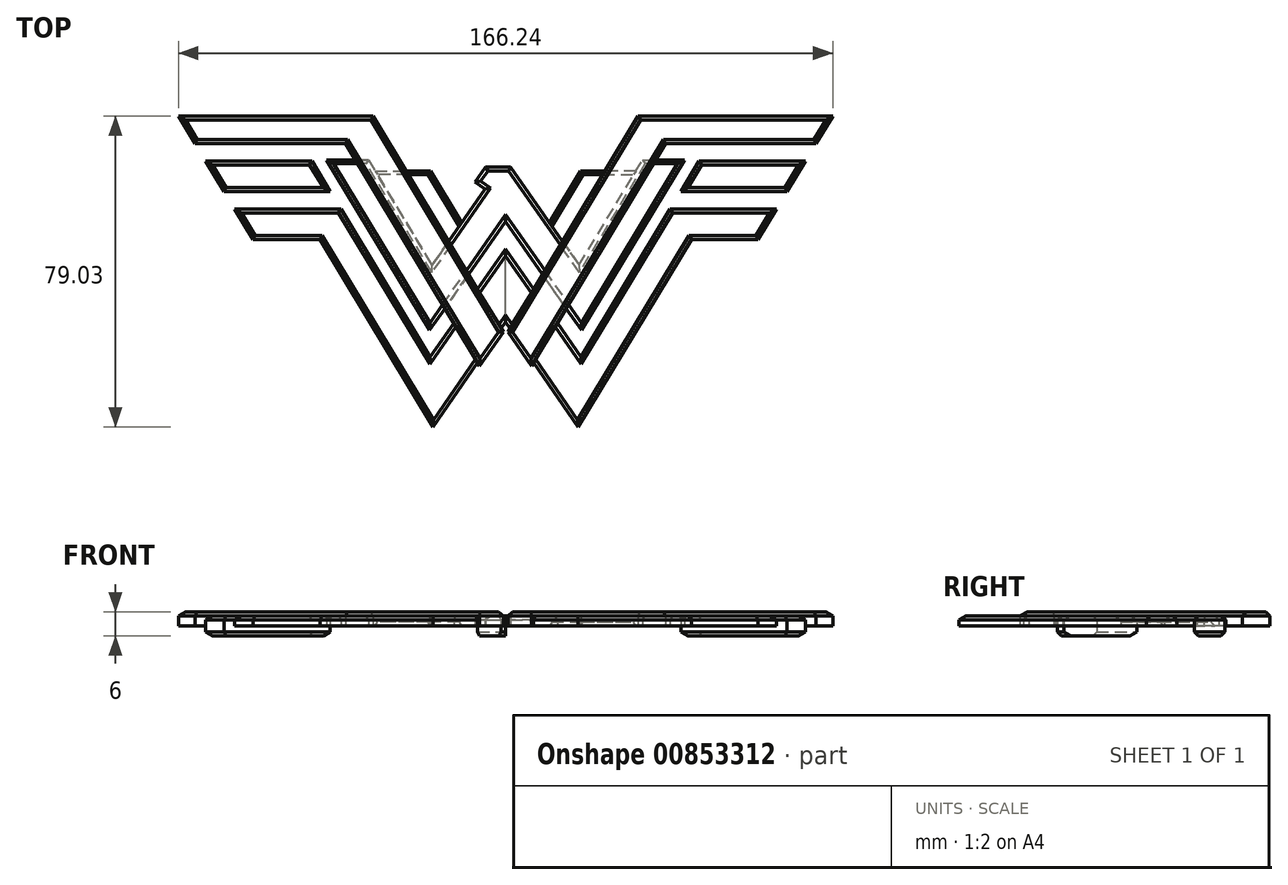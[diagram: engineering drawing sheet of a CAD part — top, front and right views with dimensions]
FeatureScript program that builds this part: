
annotation { "Feature Type Name" : "Feature", "Feature Type Description" : "" }
export const myFeature = defineFeature(function(context is Context, id is Id, definition is map)
    precondition{}
    {
        {
            var Q0;
            Q0=qCreatedBy(makeId("Top.planeOp"),FACE);
            var sketch = newSketch(context, id + "F0", { "sketchPlane" : qUnion([Q0])});
            skLineSegment(sketch, "E0", {"start": v(-1.3, 32.97) * mm, "end": v(-18.68, 8.07) * mm});
            skLineSegment(sketch, "E1", {"start": v(-18.68, 8.07) * mm, "end": v(-34.82, 34.82) * mm});
            skLineSegment(sketch, "E2", {"start": v(-34.82, 34.82) * mm, "end": v(-45.43, 34.82) * mm});
            skLineSegment(sketch, "E3", {"start": v(-45.43, 34.82) * mm, "end": v(-29.28, 8.07) * mm});
            skLineSegment(sketch, "E4", {"start": v(-29.28, 8.07) * mm, "end": v(-24.4, 0) * mm});
            skLineSegment(sketch, "E5", {"start": v(-24.4, 0) * mm, "end": v(-19.3, -8.47) * mm});
            skLineSegment(sketch, "E6", {"start": v(-19.3, -8.47) * mm, "end": v(0, 19.16) * mm});
            skLineSegment(sketch, "E7", {"start": v(0, 19.16) * mm, "end": v(0, 32.97) * mm});
            skLineSegment(sketch, "E8", {"start": v(-33.13, 32.02) * mm, "end": v(-19.08, 32.02) * mm});
            skLineSegment(sketch, "E9", {"start": v(-19.08, 32.02) * mm, "end": v(-11.14, 18.87) * mm});
            skLineSegment(sketch, "E10.MirrorCS", {"start": v(1.3, 32.97) * mm, "end": v(18.68, 8.07) * mm});
            skLineSegment(sketch, "E11.MirrorCS", {"start": v(19.3, -8.47) * mm, "end": v(0, 19.16) * mm});
            skLineSegment(sketch, "E12.MirrorCS", {"start": v(29.28, 8.07) * mm, "end": v(24.4, 0) * mm});
            skLineSegment(sketch, "E13.MirrorCS", {"start": v(24.4, 0) * mm, "end": v(19.3, -8.47) * mm});
            skLineSegment(sketch, "E14.MirrorCS", {"start": v(45.43, 34.82) * mm, "end": v(29.28, 8.07) * mm});
            skLineSegment(sketch, "E15.MirrorCS", {"start": v(34.82, 34.82) * mm, "end": v(45.43, 34.82) * mm});
            skLineSegment(sketch, "E16.MirrorCS", {"start": v(18.68, 8.07) * mm, "end": v(34.82, 34.82) * mm});
            skLineSegment(sketch, "E17", {"start": v(1.3, 32.97) * mm, "end": v(-5.04, 32.97) * mm});
            skLineSegment(sketch, "E18", {"start": v(-5.04, 32.97) * mm, "end": v(-7.72, 29.14) * mm});
            skLineSegment(sketch, "E19", {"start": v(-7.72, 29.14) * mm, "end": v(-5.2, 27.38) * mm});
            skPoint(sketch, "E20.orphan", {"position": v(0, 34.82) * mm});
            skSolve(sketch);
        }
        {
            var Q0;
            Q0=qCreatedBy(makeId("Top.planeOp"),FACE);
            var sketch = newSketch(context, id + "F1", { "sketchPlane" : qUnion([Q0])});
            skLineSegment(sketch, "E21", {"start": v(-49.18, 34.5) * mm, "end": v(-76.17, 34.5) * mm});
            skLineSegment(sketch, "E22", {"start": v(-76.17, 34.5) * mm, "end": v(-71.52, 26.8) * mm});
            skLineSegment(sketch, "E23", {"start": v(-71.52, 26.8) * mm, "end": v(-44.53, 26.8) * mm});
            skLineSegment(sketch, "E24", {"start": v(-44.53, 26.8) * mm, "end": v(-49.18, 34.5) * mm});
            skLineSegment(sketch, "E25", {"start": v(-68.81, 22.32) * mm, "end": v(-41.82, 22.32) * mm});
            skLineSegment(sketch, "E26", {"start": v(-41.82, 22.32) * mm, "end": v(-37.17, 14.62) * mm});
            skLineSegment(sketch, "E27", {"start": v(-37.17, 14.62) * mm, "end": v(-64.16, 14.62) * mm});
            skLineSegment(sketch, "E28", {"start": v(-64.16, 14.62) * mm, "end": v(-68.81, 22.32) * mm});
            skLineSegment(sketch, "E29", {"start": v(-71.52, 26.8) * mm, "end": v(-68.81, 22.32) * mm, "construction": true});
            skLineSegment(sketch, "E30", {"start": v(-44.53, 26.8) * mm, "end": v(-41.82, 22.32) * mm, "construction": true});
            skLineSegment(sketch, "E31", {"start": v(-47.17, 14.62) * mm, "end": v(-19.15, -31.8) * mm});
            skLineSegment(sketch, "E32", {"start": v(0, -3.25) * mm, "end": v(0, 12.18) * mm});
            skLineSegment(sketch, "E33", {"start": v(0, 12.18) * mm, "end": v(-19.15, -15.24) * mm});
            skLineSegment(sketch, "E34", {"start": v(-19.15, -15.24) * mm, "end": v(-37.17, 14.62) * mm});
            skLineSegment(sketch, "E35", {"start": v(-37.17, 14.62) * mm, "end": v(-47.17, 14.62) * mm});
            skLineSegment(sketch, "E36", {"start": v(-19.15, -31.8) * mm, "end": v(-18.37, -33.1) * mm});
            skLineSegment(sketch, "E37", {"start": v(-18.37, -33.1) * mm, "end": v(0, -6.41) * mm});
            skLineSegment(sketch, "E38", {"start": v(0, -6.41) * mm, "end": v(0, -3.25) * mm});
            skLineSegment(sketch, "E39", {"start": v(-78.87, 38.99) * mm, "end": v(-51.88, 38.99) * mm});
            skLineSegment(sketch, "E40", {"start": v(-51.88, 38.99) * mm, "end": v(-56.07, 45.93) * mm});
            skLineSegment(sketch, "E41", {"start": v(-56.07, 45.93) * mm, "end": v(-83.12, 45.93) * mm});
            skLineSegment(sketch, "E42", {"start": v(-83.12, 45.93) * mm, "end": v(-78.87, 38.99) * mm});
            skLineSegment(sketch, "E43", {"start": v(-51.88, 38.99) * mm, "end": v(-49.18, 34.5) * mm, "construction": true});
            skLineSegment(sketch, "E44", {"start": v(-78.87, 38.99) * mm, "end": v(-76.17, 34.5) * mm, "construction": true});
            skLineSegment(sketch, "E45", {"start": v(-56.07, 45.93) * mm, "end": v(-33.67, 45.93) * mm});
            skLineSegment(sketch, "E46", {"start": v(-33.67, 45.93) * mm, "end": v(-29.48, 38.99) * mm});
            skLineSegment(sketch, "E47", {"start": v(-29.48, 38.99) * mm, "end": v(-51.88, 38.99) * mm});
            skLineSegment(sketch, "E48", {"start": v(-40.68, 38.99) * mm, "end": v(-7.07, -16.69) * mm});
            skLineSegment(sketch, "E49", {"start": v(-29.48, 38.99) * mm, "end": v(-1.1, -8.01) * mm});
            skLineSegment(sketch, "E50", {"start": v(-1.1, -8.01) * mm, "end": v(-0.57, -8.9) * mm});
            skLineSegment(sketch, "E51", {"start": v(-0.57, -8.9) * mm, "end": v(-6.58, -17.5) * mm});
            skLineSegment(sketch, "E52", {"start": v(-6.58, -17.5) * mm, "end": v(-7.07, -16.69) * mm});
            skSolve(sketch);
        }
        {
            var Q0;
            {var subQ4=sQuery(id+"F0.wireOp",EDGE,"E8");Q0=makeQuery(id+"F0.imprint","IMPRINT",FACE,{"disambiguationData":[TD([[makeQuery(id+"F0.imprint","IMPRINT",EDGE,{"derivedFrom":subQ4}),-1.0]])]});}
            extrude(context, id + "F2", {"entities" : qUnion([Q0]), "depth" : 1 * mm, "offsetDistance" : 25 * mm});
        }
        {
            var Q0;
            Q0=makeQuery(id+"F1.imprint","IMPRINT",FACE,{"disambiguationData":[TD([[makeQuery(id+"F1.imprint","IMPRINT",EDGE,{"derivedFrom":sQuery(id+"F1.wireOp",EDGE,"E39")}),1.0]])]});
            var Q1;
            {var subQ3=sQuery(id+"F1.wireOp",EDGE,"E40");Q1=makeQuery(id+"F1.imprint","IMPRINT",FACE,{"disambiguationData":[TD([[makeQuery(id+"F1.imprint","IMPRINT",EDGE,{"derivedFrom":subQ3}),-1.0]])]});}
            var Q2;
            {var subQ0=sQuery(id+"F1.wireOp",EDGE,"E49");var subQ1=sQuery(id+"F1.wireOp",EDGE,"E33");var subQ2=makeQuery(id+"F1.imprint","INTERSECT",VERTEX,{"derivedFrom":[subQ1,subQ0]});Q2=makeQuery(id+"F1.imprint","IMPRINT",FACE,{"disambiguationData":[TD([[makeQuery(id+"F1.imprint","IMPRINT",EDGE,{"disambiguationData":[TD([[subQ2,-1.0]])],"derivedFrom":subQ1}),-1.0]])]});}
            var Q3;
            {var subQ4=sQuery(id+"F1.wireOp",EDGE,"IkarmOyA-QviY-3z2g-ssXT-DGAwllsCsLP8");Q3=makeQuery(id+"F1.imprint","IMPRINT",FACE,{"disambiguationData":[TD([[makeQuery(id+"F1.imprint","IMPRINT",EDGE,{"derivedFrom":subQ4}),-1.0]])]});}
            var Q4;
            {var subQ0=sQuery(id+"F1.wireOp",EDGE,"E49");var subQ1=sQuery(id+"F1.wireOp",EDGE,"E33");var subQ2=makeQuery(id+"F1.imprint","INTERSECT",VERTEX,{"derivedFrom":[subQ1,subQ0]});Q4=makeQuery(id+"F1.imprint","IMPRINT",FACE,{"disambiguationData":[TD([[makeQuery(id+"F1.imprint","IMPRINT",EDGE,{"disambiguationData":[TD([[subQ2,-1.0]])],"derivedFrom":subQ1}),1.0]])]});}
            var Q5;
            {var subQ2=sQuery(id+"F1.wireOp",EDGE,"E50");Q5=makeQuery(id+"F1.imprint","IMPRINT",FACE,{"disambiguationData":[TD([[makeQuery(id+"F1.imprint","IMPRINT",EDGE,{"derivedFrom":subQ2}),-1.0]])]});}
            extrude(context, id + "F3", {"entities" : qUnion([Q0, Q1, Q2, Q3, Q4, Q5]), "depth" : 3.5 * mm, "offsetDistance" : 25 * mm});
        }
        {
            var Q0;
            Q0=makeQuery(id+"F1.imprint","IMPRINT",FACE,{"disambiguationData":[TD([[makeQuery(id+"F1.imprint","IMPRINT",EDGE,{"derivedFrom":sQuery(id+"F1.wireOp",EDGE,"E25")}),-1.0]])]});
            var Q1;
            Q1=makeQuery(id+"F1.imprint","IMPRINT",FACE,{"disambiguationData":[TD([[makeQuery(id+"F1.imprint","IMPRINT",EDGE,{"derivedFrom":sQuery(id+"F1.wireOp",EDGE,"E31")}),1.0]])]});
            var Q2;
            {var subQ5=sQuery(id+"F1.wireOp",EDGE,"E32");Q2=makeQuery(id+"F1.imprint","IMPRINT",FACE,{"disambiguationData":[TD([[makeQuery(id+"F1.imprint","IMPRINT",EDGE,{"derivedFrom":subQ5}),1.0]])]});}
            extrude(context, id + "F4", {"entities" : qUnion([Q0, Q1, Q2]), "depth" : 2.5 * mm, "offsetDistance" : 25 * mm});
        }
        {
            var Q0;
            {var subQ1=sQuery(id+"F0.wireOp",EDGE,"E7");Q0=makeQuery(id+"F0.imprint","IMPRINT",FACE,{"disambiguationData":[TD([[makeQuery(id+"F0.imprint","IMPRINT",EDGE,{"derivedFrom":subQ1}),-1.0]])]});}
            var Q1;
            {var subQ0=sQuery(id+"F0.wireOp",EDGE,"E2");Q1=makeQuery(id+"F0.imprint","IMPRINT",FACE,{"disambiguationData":[TD([[makeQuery(id+"F0.imprint","IMPRINT",EDGE,{"derivedFrom":subQ0}),1.0]])]});}
            var Q2;
            {var subQ4=sQuery(id+"F0.wireOp",EDGE,"E18");Q2=makeQuery(id+"F0.imprint","IMPRINT",FACE,{"disambiguationData":[TD([[makeQuery(id+"F0.imprint","IMPRINT",EDGE,{"derivedFrom":subQ4}),1.0]])]});}
            extrude(context, id + "F5", {"entities" : qUnion([Q0, Q1, Q2]), "depth" : 2.5 * mm, "offsetDistance" : 25 * mm});
        }
        {
            var Q0;
            Q0=makeQuery(id+"F1.imprint","IMPRINT",FACE,{"disambiguationData":[TD([[makeQuery(id+"F1.imprint","IMPRINT",EDGE,{"derivedFrom":sQuery(id+"F1.wireOp",EDGE,"E21")}),1.0]])]});
            extrude(context, id + "F6", {"entities" : qUnion([Q0]), "depth" : 2.5 * mm, "offsetDistance" : 25 * mm});
        }
        {
            var Q0;
            Q0=makeQuery(id+"F3.opExtrude","CAP_FACE",FACE,{"disambiguationData":[OSD([sQuery(id+"F1.wireOp",EDGE,"E37"),sQuery(id+"F1.wireOp",EDGE,"E39"),sQuery(id+"F1.wireOp",EDGE,"E41"),sQuery(id+"F1.wireOp",EDGE,"E42"),sQuery(id+"F1.wireOp",EDGE,"E45"),sQuery(id+"F1.wireOp",EDGE,"E46"),sQuery(id+"F1.wireOp",EDGE,"E47"),sQuery(id+"F1.wireOp",EDGE,"E48"),sQuery(id+"F1.wireOp",EDGE,"E49")])],"isStart":false});
            var Q1;
            Q1=makeQuery(id+"F3.opExtrude","CAP_EDGE",EDGE,{"disambiguationData":[OSD([sQuery(id+"F1.wireOp",EDGE,"E39"),sQuery(id+"F1.wireOp",EDGE,"E47")])],"isStart":false});
            var Q2;
            {var subQ0=sQuery(id+"F1.wireOp",EDGE,"E33");Q2=makeQuery(id+"F4.opExtrude","CAP_EDGE",EDGE,{"disambiguationData":[OSD([subQ0]),TDD([makeQuery(id+"F1.imprint","IMPRINT",EDGE,{"disambiguationData":[TD([[makeQuery(id+"F1.imprint","INTERSECT",VERTEX,{"derivedFrom":[sQuery(id+"F1.wireOp",EDGE,"E32"),subQ0]}),-1.0]])],"derivedFrom":subQ0})])],"isStart":false});}
            var Q3;
            {var subQ0=sQuery(id+"F1.wireOp",EDGE,"E37");Q3=makeQuery(id+"F4.opExtrude","CAP_EDGE",EDGE,{"disambiguationData":[OSD([subQ0]),TDD([makeQuery(id+"F1.imprint","IMPRINT",EDGE,{"disambiguationData":[TD([[makeQuery(id+"F1.imprint","INTERSECT",VERTEX,{"derivedFrom":[subQ0,sQuery(id+"F1.wireOp",EDGE,"E38")]}),1.0]])],"derivedFrom":subQ0})])],"isStart":false});}
            var Q4;
            Q4=makeQuery(id+"F6.opExtrude","CAP_FACE",FACE,{"disambiguationData":[OSD([sQuery(id+"F1.wireOp",EDGE,"E21"),sQuery(id+"F1.wireOp",EDGE,"E22"),sQuery(id+"F1.wireOp",EDGE,"E23"),sQuery(id+"F1.wireOp",EDGE,"E24")])],"isStart":false});
            var Q5;
            Q5=makeQuery(id+"F4.opExtrude","CAP_EDGE",EDGE,{"disambiguationData":[OSD([sQuery(id+"F1.wireOp",EDGE,"E31"),sQuery(id+"F1.wireOp",EDGE,"E36")])],"isStart":false});
            var Q6;
            {var subQ0=sQuery(id+"F1.wireOp",EDGE,"E37");Q6=makeQuery(id+"F4.opExtrude","CAP_EDGE",EDGE,{"disambiguationData":[OSD([subQ0]),TDD([makeQuery(id+"F1.imprint","IMPRINT",EDGE,{"disambiguationData":[TD([[makeQuery(id+"F1.imprint","INTERSECT",VERTEX,{"derivedFrom":[sQuery(id+"F1.wireOp",EDGE,"E36"),subQ0]}),-1.0]])],"derivedFrom":subQ0})])],"isStart":false});}
            var Q7;
            {var subQ0=sQuery(id+"F1.wireOp",EDGE,"E33");Q7=makeQuery(id+"F4.opExtrude","CAP_EDGE",EDGE,{"disambiguationData":[OSD([subQ0]),TDD([makeQuery(id+"F1.imprint","IMPRINT",EDGE,{"disambiguationData":[TD([[makeQuery(id+"F1.imprint","INTERSECT",VERTEX,{"derivedFrom":[subQ0,sQuery(id+"F1.wireOp",EDGE,"E34")]}),1.0]])],"derivedFrom":subQ0})])],"isStart":false});}
            var Q8;
            Q8=makeQuery(id+"F4.opExtrude","CAP_EDGE",EDGE,{"disambiguationData":[OSD([sQuery(id+"F1.wireOp",EDGE,"E28")])],"isStart":false});
            var Q9;
            Q9=makeQuery(id+"F4.opExtrude","CAP_EDGE",EDGE,{"disambiguationData":[OSD([sQuery(id+"F1.wireOp",EDGE,"E27")])],"isStart":false});
            var Q10;
            Q10=makeQuery(id+"F4.opExtrude","CAP_EDGE",EDGE,{"disambiguationData":[OSD([sQuery(id+"F1.wireOp",EDGE,"E25")])],"isStart":false});
            var Q11;
            Q11=makeQuery(id+"F4.opExtrude","CAP_EDGE",EDGE,{"disambiguationData":[OSD([sQuery(id+"F1.wireOp",EDGE,"E26"),sQuery(id+"F1.wireOp",EDGE,"E34")])],"isStart":false});
            var Q12;
            Q12=makeQuery(id+"F5.opExtrude","CAP_FACE",FACE,{"disambiguationData":[OSD([sQuery(id+"F0.wireOp",EDGE,"E0"),sQuery(id+"F0.wireOp",EDGE,"E1"),sQuery(id+"F0.wireOp",EDGE,"E2"),sQuery(id+"F0.wireOp",EDGE,"E3"),sQuery(id+"F0.wireOp",EDGE,"E4"),sQuery(id+"F0.wireOp",EDGE,"E5"),sQuery(id+"F0.wireOp",EDGE,"E6"),sQuery(id+"F0.wireOp",EDGE,"E10.MirrorCS"),sQuery(id+"F0.wireOp",EDGE,"E11.MirrorCS"),sQuery(id+"F0.wireOp",EDGE,"E12.MirrorCS"),sQuery(id+"F0.wireOp",EDGE,"E13.MirrorCS"),sQuery(id+"F0.wireOp",EDGE,"E14.MirrorCS"),sQuery(id+"F0.wireOp",EDGE,"E15.MirrorCS"),sQuery(id+"F0.wireOp",EDGE,"E16.MirrorCS"),sQuery(id+"F0.wireOp",EDGE,"E17"),sQuery(id+"F0.wireOp",EDGE,"E18"),sQuery(id+"F0.wireOp",EDGE,"E19")])],"isStart":false});
            var Q13;
            Q13=makeQuery(id+"F2.opExtrude","CAP_EDGE",EDGE,{"disambiguationData":[OSD([sQuery(id+"F0.wireOp",EDGE,"E8")])],"isStart":false});
            var Q14;
            Q14=makeQuery(id+"F2.opExtrude","CAP_EDGE",EDGE,{"disambiguationData":[OSD([sQuery(id+"F0.wireOp",EDGE,"E9")])],"isStart":false});
            chamfer(context, id + "F7", {"entities" : qUnion([Q0, Q1, Q2, Q3, Q4, Q5, Q6, Q7, Q8, Q9, Q10, Q11, Q12, Q13, Q14]), "width" : 1 * mm, "tangentPropagation" : true});
        }
        {
            var Q0;
            Q0=makeQuery(id+"F4.opExtrude","SWEPT_BODY",BODY,{"disambiguationData":[OSD([sQuery(id+"F1.wireOp",EDGE,"E25"),sQuery(id+"F1.wireOp",EDGE,"E26"),sQuery(id+"F1.wireOp",EDGE,"E27"),sQuery(id+"F1.wireOp",EDGE,"E28"),sQuery(id+"F1.wireOp",EDGE,"E31"),sQuery(id+"F1.wireOp",EDGE,"E33"),sQuery(id+"F1.wireOp",EDGE,"E34"),sQuery(id+"F1.wireOp",EDGE,"E36"),sQuery(id+"F1.wireOp",EDGE,"E37"),sQuery(id+"F1.wireOp",EDGE,"E48")])]});
            var Q1;
            Q1=makeQuery(id+"F4.opExtrude","SWEPT_BODY",BODY,{"disambiguationData":[OSD([sQuery(id+"F1.wireOp",EDGE,"E32"),sQuery(id+"F1.wireOp",EDGE,"E33"),sQuery(id+"F1.wireOp",EDGE,"E37"),sQuery(id+"F1.wireOp",EDGE,"E38"),sQuery(id+"F1.wireOp",EDGE,"E49")])]});
            var Q2;
            Q2=makeQuery(id+"F3.opExtrude","SWEPT_BODY",BODY,{"disambiguationData":[OSD([sQuery(id+"F1.wireOp",EDGE,"E37"),sQuery(id+"F1.wireOp",EDGE,"E39"),sQuery(id+"F1.wireOp",EDGE,"E41"),sQuery(id+"F1.wireOp",EDGE,"E42"),sQuery(id+"F1.wireOp",EDGE,"E45"),sQuery(id+"F1.wireOp",EDGE,"E46"),sQuery(id+"F1.wireOp",EDGE,"E47"),sQuery(id+"F1.wireOp",EDGE,"E48"),sQuery(id+"F1.wireOp",EDGE,"E49")])]});
            var Q3;
            Q3=makeQuery(id+"F2.opExtrude","SWEPT_BODY",BODY,{"disambiguationData":[OSD([sQuery(id+"F0.wireOp",EDGE,"E0"),sQuery(id+"F0.wireOp",EDGE,"E1"),sQuery(id+"F0.wireOp",EDGE,"E8"),sQuery(id+"F0.wireOp",EDGE,"E9")])]});
            var Q4;
            Q4=makeQuery(id+"F6.opExtrude","SWEPT_BODY",BODY,{"disambiguationData":[OSD([sQuery(id+"F1.wireOp",EDGE,"E21"),sQuery(id+"F1.wireOp",EDGE,"E22"),sQuery(id+"F1.wireOp",EDGE,"E23"),sQuery(id+"F1.wireOp",EDGE,"E24")])]});
            var Q5;
            Q5=qCreatedBy(makeId("Right.planeOp"),FACE);
            mirror(context, id + "F8", {"entities" : qUnion([Q0, Q1, Q2, Q3, Q4]), "mirrorPlane" : qUnion([Q5])});
        }
        {
            var Q0;
            Q0=makeQuery(id+"F4.opExtrude","SWEPT_BODY",BODY,{"disambiguationData":[OSD([sQuery(id+"F1.wireOp",EDGE,"E32"),sQuery(id+"F1.wireOp",EDGE,"E33"),sQuery(id+"F1.wireOp",EDGE,"E37"),sQuery(id+"F1.wireOp",EDGE,"E38"),sQuery(id+"F1.wireOp",EDGE,"E49")])]});
            var Q1;
            Q1=makeQuery(id+"F6.opExtrude","SWEPT_BODY",BODY,{"disambiguationData":[OSD([sQuery(id+"F1.wireOp",EDGE,"E21"),sQuery(id+"F1.wireOp",EDGE,"E22"),sQuery(id+"F1.wireOp",EDGE,"E23"),sQuery(id+"F1.wireOp",EDGE,"E24")])]});
            var Q2;
            Q2=makeQuery(id+"F8.opPattern","COPY",BODY,{"derivedFrom":makeQuery(id+"F6.opExtrude","SWEPT_BODY",BODY,{"disambiguationData":[OSD([sQuery(id+"F1.wireOp",EDGE,"E21"),sQuery(id+"F1.wireOp",EDGE,"E22"),sQuery(id+"F1.wireOp",EDGE,"E23"),sQuery(id+"F1.wireOp",EDGE,"E24")])]}),"instanceName":"1"});
            var Q3;
            Q3=qCreatedBy(makeId("Top.planeOp"),FACE);
            mirror(context, id + "F9", {"operationType" : NewBodyOperationType.ADD, "entities" : qUnion([Q0, Q1, Q2]), "mirrorPlane" : qUnion([Q3])});
        }
    });
